# Revit family: Metal_Lockers-Salsbury_Industries-63000_Series-1_Wide_Units
name_source: partatom
category: Specialty Equipment
revit_build: Autodesk Revit 2016 (Build: 20150714_1515(x64)
units: mm (PartAtom-declared; Revit-internal decimal feet)

## family parameters
Always vertical = Yes
Cut with Voids When Loaded = No
OmniClass Number = 23.40.00.00
OmniClass Title = Equipment and Furnishings
Part Type = Normal
Room Calculation Point = No
Round Connector Dimension = Use Diameter
Shared = No
Work Plane-Based = No

## types (18) — shared parameters
Assembly Code = C1030310
Door Location D1 = Metal Locker Doors-12 inch with Hasps : Triple Tier Door - 6 foot
Hasp Handle Material = Plastic - Salsbury Finish - Black
Hasp Plate Rivet Material = Steel -Salsbury Finish - Polished Steel
Manufacturer = Salsbury Industries
MasterFormat Number = 10 51 13
MasterFormat Title = Lockers
OmniClass 23 Number = 23.40.00.00
OmniClass 23 Title = Equipment and Furnishings
Standard Leg Base = Metal Locker Legs : 6" High - 12" W x 12" D
Type Comments = Standard Metal Locker - Triple Tier
URL = www.lockers.com
Version = 2.0 (06/30/17)
Width = 12.04 "
Zee Base = Metal Locker Zee Base : None

## per-type parameters (varying)
| type | Base Height | Compartment Divider Height | Depth | Description | Individual Door Height | Model | Sloping Hood Height | Unit Height |
| 63162 - with Standard 6" High Legs | 6 " | 22.814 " | 12.01 " | 1 Wide - 6 Feet High - 12 Inches Deep | 23.189 " | 63162 | 6.625 " | 72 " |
| 63165 - with Standard 6" High Legs | 6 " | 22.814 " | 15.01 " | 1 Wide - 6 Feet High - 15 Inches Deep | 23.189 " | 63165 | 8.682 " | 72 " |
| 63168 - with Standard 6" High Legs | 6 " | 22.814 " | 18.01 " | 1 Wide - 6 Feet High - 18 Inches Deep | 23.189 " | 63168 | 10.739 " | 72 " |
| 63162 - with 77572 Zee Base and 77550 Lockers without Legs | 4 " | 22.814 " | 12.01 " | 1 Wide - 6 Feet High - 12 Inches Deep with Zee Base and Lockers without Legs | 23.189 " | 63162 with 77572 and 77550 | 6.625 " | 72 " |
| 63165 - with 77575 Zee Base and 77550 Lockers without Legs | 4 " | 22.814 " | 15.01 " | 1 Wide - 6 Feet High - 15 Inches Deep with Zee Base and Lockers without Legs | 23.189 " | 63165 with 77575 and 77550 | 8.682 " | 72 " |
| 63168 - with 77578 Zee Base and 77550 Lockers without Legs | 4 " | 22.814 " | 18.01 " | 1 Wide - 6 Feet High - 18 Inches Deep with Zee Base and Lockers without Legs | 23.189 " | 63168 with 77578 and 77550 | 10.739 " | 72 " |
| 63162 - with 77550 Lockers without Legs | 0 " | 22.814 " | 12.01 " | 1 Wide - 6 Feet High - 12 Inches Deep with Lockers without Legs | 23.189 " | 63162 with 77550 | 6.625 " | 72 " |
| 63165 - with 77550 Lockers without Legs | 0 " | 22.814 " | 15.01 " | 1 Wide - 6 Feet High - 15 Inches Deep with Lockers without Legs | 23.189 " | 63165 with 77550 | 8.682 " | 72 " |
| 63168 - with 77550 Lockers without Legs | 0 " | 22.814 " | 18.01 " | 1 Wide - 6 Feet High - 18 Inches Deep with Lockers without Legs | 23.189 " | 63168 with 77550 | 10.739 " | 72 " |
| 63152 - with Standard 6" High Legs | 6 " | 18.814 " | 12.01 " | 1 Wide - 5 Feet High - 12 Inches Deep | 19.189 " | 63152 | 6.625 " | 60 " |
| 63152 - with 77572 Zee Base and 77550 Lockers without Legs | 4 " | 18.814 " | 12.01 " | 1 Wide - 5 Feet High - 12 Inches Deep with Zee Base and Lockers without Legs | 19.189 " | 63152 with 77572 and 77550 | 6.625 " | 60 " |
| 63152 - with 77550 Lockers without Legs | 0 " | 18.814 " | 12.01 " | 1 Wide - 5 Feet High - 12 Inches Deep with Lockers without Legs | 19.189 " | 63152 with 77550 | 6.625 " | 60 " |
| 63155 - with Standard 6" High Legs | 6 " | 18.814 " | 15.01 " | 1 Wide - 5 Feet High - 15 Inches Deep | 19.189 " | 63155 | 8.682 " | 60 " |
| 63155 - with 77575 Zee Base and 77550 Lockers without Legs | 4 " | 18.814 " | 15.01 " | 1 Wide - 5 Feet High - 15 Inches Deep with Zee Base and Lockers without Legs | 19.189 " | 63155 with 77575 and 77550 | 8.682 " | 60 " |
| 63155 - with 77550 Lockers without Legs | 0 " | 18.814 " | 15.01 " | 1 Wide - 5 Feet High - 15 Inches Deep with Lockers without Legs | 19.189 " | 63165 with 77550 | 8.682 " | 60 " |
| 63158 - with Standard 6" High Legs | 6 " | 18.814 " | 18.01 " | 1 Wide - 5 Feet High - 18 Inches Deep | 19.189 " | 63158 | 10.739 " | 60 " |
| 63158 - with 77578 Zee Base and 77550 Lockers without Legs | 4 " | 18.814 " | 18.01 " | 1 Wide - 5 Feet High - 18 Inches Deep with Zee Base and Lockers without Legs | 19.189 " | 63158 with 77578 and 77550 | 10.739 " | 60 " |
| 63158 - with 77550 Lockers without Legs | 0 " | 18.814 " | 18.01 " | 1 Wide - 5 Feet High - 18 Inches Deep with Lockers without Legs | 19.189 " | 63158 with 77550 | 10.739 " | 60 " |

## geometry (parser evidence)
native form markers: Sweep x46
no freeform markers — native parametric forms only
